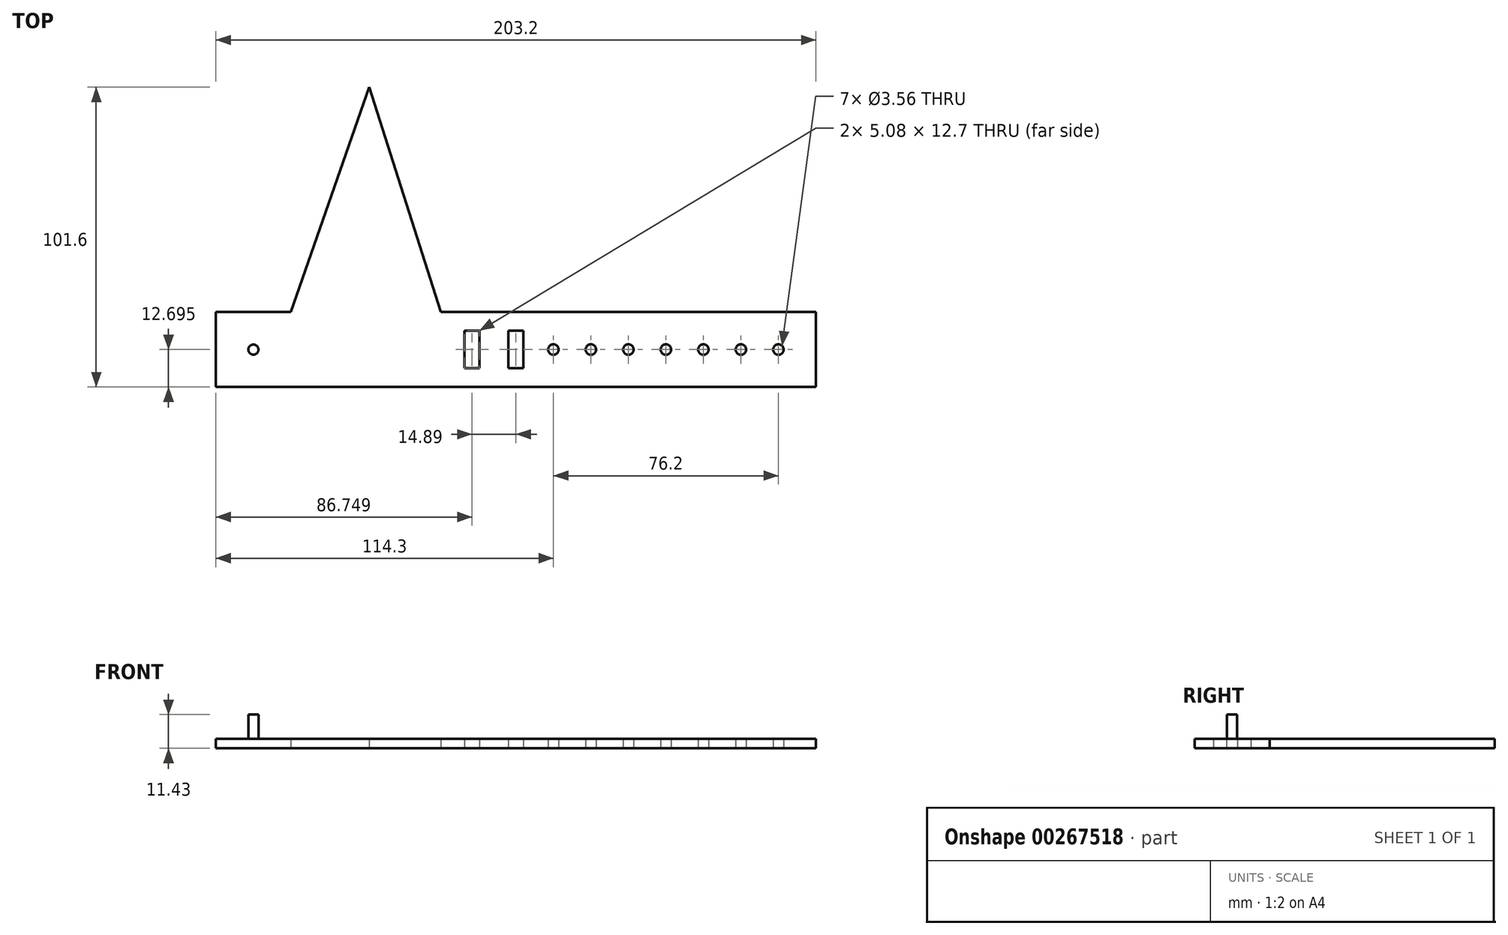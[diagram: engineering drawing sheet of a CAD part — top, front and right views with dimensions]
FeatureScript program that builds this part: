
annotation { "Feature Type Name" : "Feature", "Feature Type Description" : "" }
export const myFeature = defineFeature(function(context is Context, id is Id, definition is map)
    precondition{}
    {
        {
            var Q0;
            Q0=qCreatedBy(makeId("Top.planeOp"),FACE);
            var sketch = newSketch(context, id + "F0", { "sketchPlane" : qUnion([Q0])});
            skLineSegment(sketch, "E0.top", {"start": v(-63.65, -9.63) * mm, "end": v(139.55, -9.63) * mm});
            skLineSegment(sketch, "E0.right", {"start": v(139.55, 15.77) * mm, "end": v(139.55, -9.63) * mm});
            skLineSegment(sketch, "E1", {"start": v(-38.25, -9.63) * mm, "end": v(-38.25, 15.76) * mm});
            skPoint(sketch, "E2", {"position": v(88.75, 3.06) * mm});
            skPoint(sketch, "E3", {"position": v(101.45, 3.06) * mm});
            skPoint(sketch, "E4", {"position": v(126.85, 3.06) * mm});
            skCircle(sketch, "E5", {"center": v(50.65, 3.06) * mm, "radius": 1.78 * mm});
            skCircle(sketch, "E6", {"center": v(63.35, 3.06) * mm, "radius": 1.78 * mm});
            skCircle(sketch, "E7", {"center": v(76.05, 3.06) * mm, "radius": 1.78 * mm});
            skCircle(sketch, "E8", {"center": v(88.75, 3.06) * mm, "radius": 1.78 * mm});
            skCircle(sketch, "E9", {"center": v(101.45, 3.06) * mm, "radius": 1.78 * mm});
            skCircle(sketch, "E10", {"center": v(114.15, 3.06) * mm, "radius": 1.78 * mm});
            skCircle(sketch, "E11", {"center": v(126.85, 3.06) * mm, "radius": 1.78 * mm});
            skLineSegment(sketch, "E12", {"start": v(-63.65, 15.77) * mm, "end": v(-63.65, -9.63) * mm});
            skCircle(sketch, "E13", {"center": v(-50.95, 3.06) * mm, "radius": 1.71 * mm});
            skLineSegment(sketch, "E14", {"start": v(-44.6, 15.77) * mm, "end": v(-44.6, -9.63) * mm});
            skLineSegment(sketch, "E15", {"start": v(-63.65, 15.77) * mm, "end": v(139.55, 15.77) * mm});
            skPoint(sketch, "E16", {"position": v(23.1, 3.06) * mm});
            skPoint(sketch, "E17", {"position": v(37.99, 3.06) * mm});
            skLineSegment(sketch, "E18", {"start": v(20.56, 3.06) * mm, "end": v(20.56, 9.41) * mm});
            skLineSegment(sketch, "E19", {"start": v(20.56, 9.41) * mm, "end": v(25.64, 9.41) * mm});
            skLineSegment(sketch, "E20", {"start": v(25.64, 9.41) * mm, "end": v(25.64, -3.29) * mm});
            skLineSegment(sketch, "E21", {"start": v(25.64, -3.29) * mm, "end": v(20.56, -3.29) * mm});
            skLineSegment(sketch, "E22", {"start": v(20.56, -3.29) * mm, "end": v(20.56, 3.06) * mm});
            skLineSegment(sketch, "E23", {"start": v(35.45, 3.06) * mm, "end": v(35.45, 9.41) * mm});
            skLineSegment(sketch, "E24", {"start": v(35.45, 9.41) * mm, "end": v(40.53, 9.41) * mm});
            skLineSegment(sketch, "E25", {"start": v(40.53, 9.41) * mm, "end": v(40.53, -3.29) * mm});
            skLineSegment(sketch, "E26", {"start": v(40.53, -3.29) * mm, "end": v(35.45, -3.29) * mm});
            skLineSegment(sketch, "E27", {"start": v(35.45, -3.29) * mm, "end": v(35.45, 3.06) * mm});
            skPoint(sketch, "E28", {"position": v(-11.7, 15.77) * mm});
            skPoint(sketch, "E29", {"position": v(12.55, 15.76) * mm});
            skPoint(sketch, "E30", {"position": v(-38.25, 15.76) * mm});
            skLineSegment(sketch, "E31", {"start": v(-11.7, 15.77) * mm, "end": v(-11.7, 91.97) * mm});
            skLineSegment(sketch, "E32", {"start": v(-11.7, 91.97) * mm, "end": v(12.55, 15.76) * mm});
            skLineSegment(sketch, "E33", {"start": v(-11.7, 91.97) * mm, "end": v(-38.25, 15.76) * mm});
            skSolve(sketch);
        }
        {
            var Q0;
            {var subQ1=sQuery(id+"F0.wireOp",EDGE,"E0.right");Q0=makeQuery(id+"F0.imprint","IMPRINT",FACE,{"disambiguationData":[TD([[makeQuery(id+"F0.imprint","IMPRINT",EDGE,{"derivedFrom":subQ1}),-1.0]])]});}
            var Q1;
            {var subQ0=sQuery(id+"F0.wireOp",EDGE,"E1");Q1=makeQuery(id+"F0.imprint","IMPRINT",FACE,{"disambiguationData":[TD([[makeQuery(id+"F0.imprint","IMPRINT",EDGE,{"derivedFrom":subQ0}),1.0]])]});}
            var Q2;
            {var subQ2=sQuery(id+"F0.wireOp",EDGE,"ESiy6eZe-AyIQ-knfH-7eOx-MM8NUpnfnsBf");Q2=makeQuery(id+"F0.imprint","IMPRINT",FACE,{"disambiguationData":[TD([[makeQuery(id+"F0.imprint","IMPRINT",EDGE,{"derivedFrom":subQ2}),1.0]])]});}
            var Q3;
            {var subQ0=sQuery(id+"F0.wireOp",EDGE,"ESiy6eZe-AyIQ-knfH-7eOx-MM8NUpnfnsBf");Q3=makeQuery(id+"F0.imprint","IMPRINT",FACE,{"disambiguationData":[TD([[makeQuery(id+"F0.imprint","IMPRINT",EDGE,{"derivedFrom":subQ0}),-1.0]])]});}
            var Q4;
            {var subQ0=sQuery(id+"F0.wireOp",EDGE,"E12");Q4=makeQuery(id+"F0.imprint","IMPRINT",FACE,{"disambiguationData":[TD([[makeQuery(id+"F0.imprint","IMPRINT",EDGE,{"derivedFrom":subQ0}),1.0]])]});}
            var Q5;
            {var subQ0=sQuery(id+"F0.wireOp",EDGE,"E31");Q5=makeQuery(id+"F0.imprint","IMPRINT",FACE,{"disambiguationData":[TD([[makeQuery(id+"F0.imprint","IMPRINT",EDGE,{"derivedFrom":subQ0}),1.0]])]});}
            var Q6;
            {var subQ0=sQuery(id+"F0.wireOp",EDGE,"E31");Q6=makeQuery(id+"F0.imprint","IMPRINT",FACE,{"disambiguationData":[TD([[makeQuery(id+"F0.imprint","IMPRINT",EDGE,{"derivedFrom":subQ0}),-1.0]])]});}
            extrude(context, id + "F1", {"entities" : qUnion([Q0, Q1, Q2, Q3, Q4, Q5, Q6]), "depth" : 3.17 * mm});
        }
        {
            var Q0;
            Q0=makeQuery(id+"F0.imprint","IMPRINT",FACE,{"disambiguationData":[TD([[makeQuery(id+"F0.imprint","IMPRINT",EDGE,{"derivedFrom":sQuery(id+"F0.wireOp",EDGE,"E13")}),1.0]])]});
            extrude(context, id + "F2", {"entities" : qUnion([Q0]), "operationType" : NewBodyOperationType.ADD, "depth" : 11.43 * mm});
        }
    });
